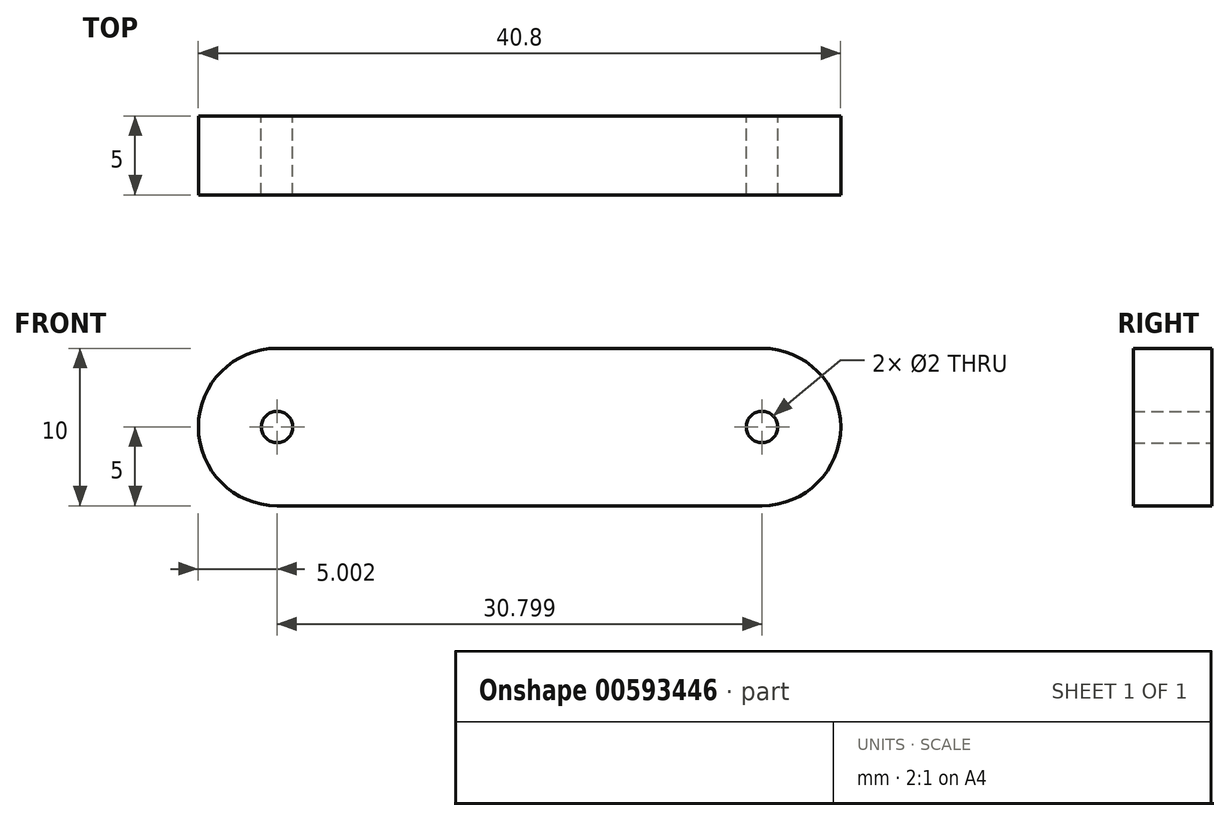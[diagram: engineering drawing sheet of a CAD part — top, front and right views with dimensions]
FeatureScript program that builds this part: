
annotation { "Feature Type Name" : "Feature", "Feature Type Description" : "" }
export const myFeature = defineFeature(function(context is Context, id is Id, definition is map)
    precondition{}
    {
        {
            assignVariable(context, id + "F0", {"name" : "bar2_depth", "anyValue" : 5});
        }
        {
            assignVariable(context, id + "F1", {"name" : "bar2_hole", "anyValue" : 2});
        }
        {
            var Q0;
            Q0=qCreatedBy(makeId("Front.planeOp"),FACE);
            var sketch = newSketch(context, id + "F2", { "sketchPlane" : qUnion([Q0])});
            skLineSegment(sketch, "E0", {"start": v(-29.04, 0) * mm, "end": v(31.18, 0) * mm, "construction": true});
            skLineSegment(sketch, "E1", {"start": v(-8.04, 5) * mm, "end": v(-8.04, -17.78) * mm, "construction": true});
            skCircle(sketch, "E2.MirrorC", {"center": v(12.96, 0) * mm, "radius": 5 * mm});
            skPoint(sketch, "E3", {"position": v(-17.84, 0) * mm});
            skCircle(sketch, "E4", {"center": v(-17.84, 0) * mm, "radius": 5 * mm});
            skLineSegment(sketch, "E5", {"start": v(12.96, 5) * mm, "end": v(-17.84, 5) * mm});
            skLineSegment(sketch, "E6", {"start": v(-17.84, -5) * mm, "end": v(12.96, -5) * mm});
            skSolve(sketch);
        }
        {
            var Q0;
            Q0 = qSketchRegion(id + "F2", true);
            extrude(context, id + "F3", {"entities" : qUnion([Q0]), "depth" : (getVariable(context, 'bar2_depth')) * mm, "offsetDistance" : 25 * mm});
        }
        {
            var Q0;
            Q0=sQuery(id+"F2.wireOp",VERTEX,"ir8tG1De-JqOu-1o0d-j0MN-l6wTs2xbIzAH.center");
            var Q1;
            Q1=sQuery(id+"F2.wireOp",VERTEX,"E2.MirrorC.center");
            var Q2;
            Q2=makeQuery(id+"F3.opExtrude","SWEPT_BODY",BODY,{"disambiguationData":[OSD([sQuery(id+"F2.wireOp",EDGE,"wh3rVfz8-rpLg-tWO1-hIX9-0KUOkSmqS98V"),sQuery(id+"F2.wireOp",EDGE,"b98c4478-69e3-45e6-be3f-00a3511e570f0.MirrorCS"),sQuery(id+"F2.wireOp",EDGE,"ir8tG1De-JqOu-1o0d-j0MN-l6wTs2xbIzAH"),sQuery(id+"F2.wireOp",EDGE,"E2.MirrorC")])]});
            hole(context, id + "F4", {"style" : HoleStyle.SIMPLE, "endStyle" : HoleEndStyle.THROUGH, "oppositeDirection" : true, "holeDiameter" : (getVariable(context, 'bar2_hole')) * mm, "majorDiameter" : 5 * mm, "isTappedThrough" : true, "tappedDepth" : 12.7 * mm, "tapClearance" : 3, "locations" : qUnion([Q0, Q1]), "scope" : qUnion([Q2])});
        }
        {
            var Q0;
            Q0=sQuery(id+"F2.wireOp",VERTEX,"E3");
            var Q1;
            Q1=makeQuery(id+"F3.opExtrude","SWEPT_BODY",BODY,{"disambiguationData":[OSD([sQuery(id+"F2.wireOp",EDGE,"wh3rVfz8-rpLg-tWO1-hIX9-0KUOkSmqS98V"),sQuery(id+"F2.wireOp",EDGE,"b98c4478-69e3-45e6-be3f-00a3511e570f0.MirrorCS"),sQuery(id+"F2.wireOp",EDGE,"ir8tG1De-JqOu-1o0d-j0MN-l6wTs2xbIzAH"),sQuery(id+"F2.wireOp",EDGE,"E2.MirrorC")])]});
            hole(context, id + "F5", {"style" : HoleStyle.SIMPLE, "endStyle" : HoleEndStyle.THROUGH, "oppositeDirection" : true, "holeDiameter" : (getVariable(context, 'bar2_hole')) * mm, "majorDiameter" : 5 * mm, "isTappedThrough" : true, "tappedDepth" : 12.7 * mm, "tapClearance" : 3, "locations" : qUnion([Q0]), "scope" : qUnion([Q1])});
        }
    });
